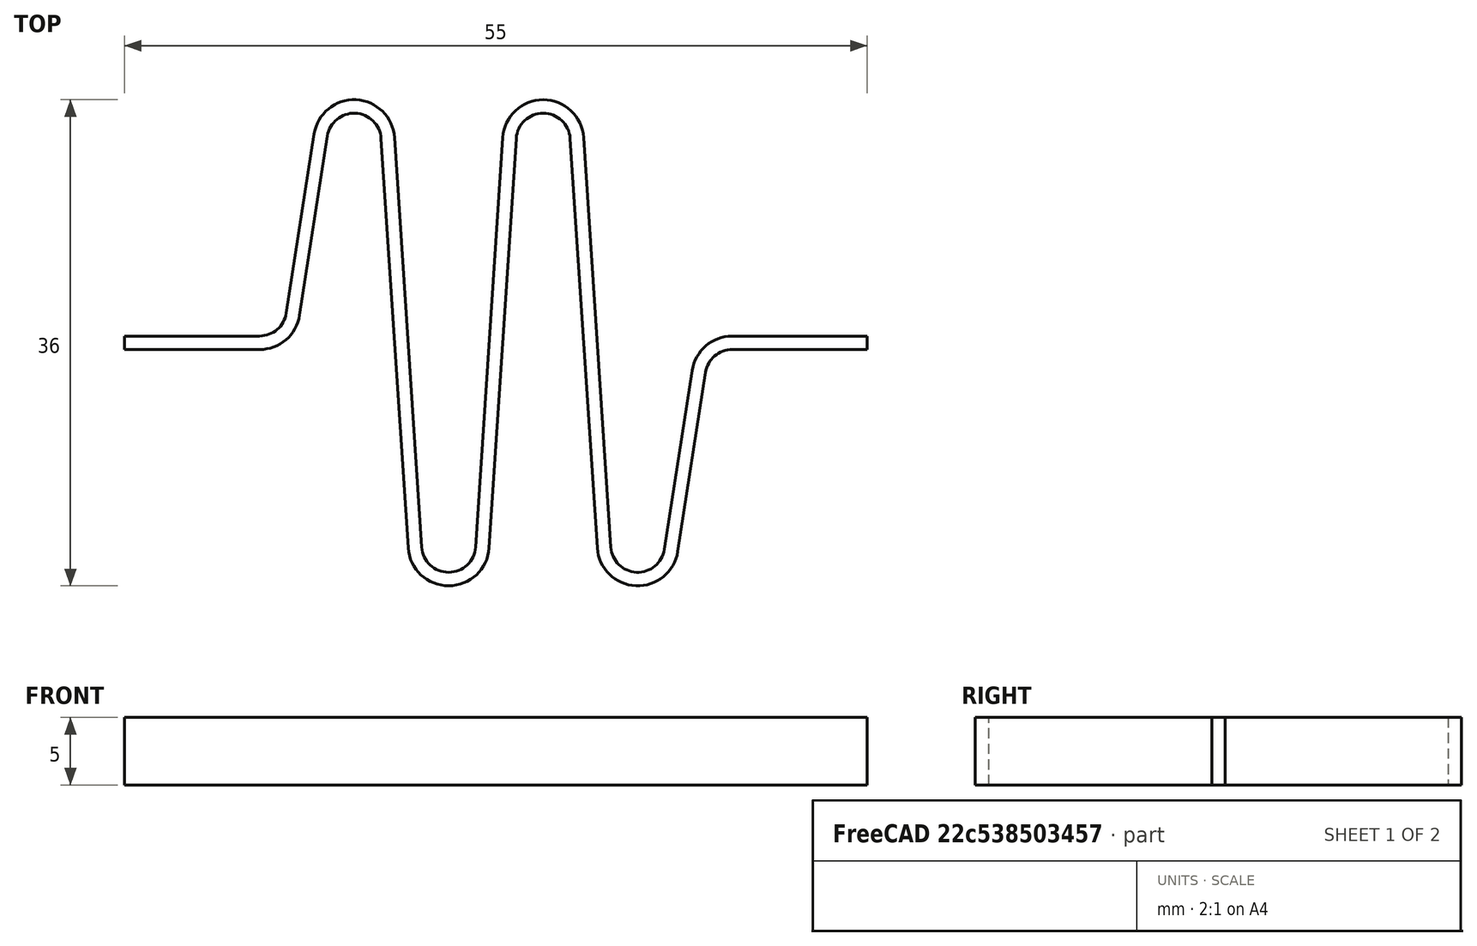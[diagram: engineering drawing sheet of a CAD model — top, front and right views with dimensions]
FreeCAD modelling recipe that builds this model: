
FCSTD DOCUMENT  (FreeCAD 2021.1015R24301 +3962 (Git))
Label: plastic_spring_1
License: All rights reserved
objects: Sketcher::SketchObject×2, Spreadsheet::Sheet×1, PartDesign::AdditivePipe×1, PartDesign::Body×1
note: 6 computed .brp shape members not serialized (recipe doc carries the construction recipe); baked Part::Feature solids carry a one-line shape summary decoded from their .brp

FEATURE [Spreadsheet::Sheet] Spreadsheet
  PythonMode = false
  cells = A1='height; B1(h)=5; A2='thickness; B2(thk)=1; A3='dia; B3(dia)=5; A4=center length; B4(l_center)=30; A5=center spacing; B5(cs)=7; C5=should be dia/2 really; A6=end length; B6(l_end)=10
FEATURE [Sketcher::SketchObject] Sketch  label="profile"
  FullyConstrained = true
  MapMode = 5
  Placement = pos=(0,0,0) rot=(0.57735,0.57735,0.57735;2.0944rad)
  Support = -> [YZ_Plane]
  expr: Constraints[10] = Spreadsheet.thk / 2
  expr: Constraints[11] = Spreadsheet.thk
  expr: Constraints[9] = Spreadsheet.h
  sketch-geometry (4):
    g0: LineSegment StartX=-0.5 StartY=0 StartZ=0 EndX=0.5 EndY=0 EndZ=0
    g1: LineSegment StartX=0.5 StartY=0 StartZ=0 EndX=0.5 EndY=5 EndZ=0
    g2: LineSegment StartX=0.5 StartY=5 StartZ=0 EndX=-0.5 EndY=5 EndZ=0
    g3: LineSegment StartX=-0.5 StartY=5 StartZ=0 EndX=-0.5 EndY=0 EndZ=0
  constraints (12):
    c: Coincident(g0,g1)
    c: Coincident(g1,g2)
    c: Coincident(g2,g3)
    c: Coincident(g3,g0)
    c: Horizontal(g0)
    c: Horizontal(g2)
    c: Vertical(g1)
    c: Vertical(g3)
    c: PointOnObject(g0,g-1)
    c: DistanceY(g3,g3) = 5
    c: DistanceX(g0,g-1) = 0.5
    c: DistanceX(g0,g0) = 1
FEATURE [Sketcher::SketchObject] Sketch001  label="path"
  FullyConstrained = false
  MapMode = 5
  Support = -> [XY_Plane]
  expr: Constraints[28] = Spreadsheet.l_end
  expr: Constraints[33] = Spreadsheet.l_center / 2
  expr: Constraints[34] = Spreadsheet.l_center
  expr: Constraints[39] = Spreadsheet.dia
  expr: Constraints[40] = Spreadsheet.dia
  expr: Constraints[41] = Spreadsheet.dia
  expr: Constraints[42] = Spreadsheet.dia
  expr: Constraints[43] = Spreadsheet.dia
  expr: Constraints[44] = Spreadsheet.dia
  expr: Constraints[45] = Spreadsheet.l_end
  expr: Constraints[46] = Spreadsheet.cs
  expr: Constraints[47] = Spreadsheet.cs
  expr: Constraints[48] = Spreadsheet.cs
  expr: Constraints[49] = Spreadsheet.cs
  expr: Constraints[50] = Spreadsheet.cs
  sketch-geometry (15):
    g0: LineSegment StartX=0 StartY=0 StartZ=0 EndX=10 EndY=0 EndZ=0
    g1: LineSegment StartX=12.4704 StartY=2.11657 StartZ=0 EndX=14.5296 EndY=15.3834 EndZ=0
    g2: ArcOfCircle CenterX=9.99998 CenterY=2.5 CenterZ=0 NormalX=0 NormalY=0 NormalZ=1 AngleXU=0 Radius=2.5 StartAngle=4.7124 EndAngle=6.1292
    g3: ArcOfCircle CenterX=17 CenterY=15 CenterZ=0 NormalX=0 NormalY=0 NormalZ=1 AngleXU=0 Radius=2.5 StartAngle=0.0662045 EndAngle=2.98761
    g4: LineSegment StartX=19.4945 StartY=15.1654 StartZ=0 EndX=21.5055 EndY=-15.1654 EndZ=0
    g5: ArcOfCircle CenterX=24 CenterY=-15 CenterZ=0 NormalX=0 NormalY=0 NormalZ=1 AngleXU=0 Radius=2.5 StartAngle=3.2078 EndAngle=6.21698
    g6: LineSegment StartX=26.4945 StartY=-15.1654 StartZ=0 EndX=28.5055 EndY=15.1654 EndZ=0
    g7: ArcOfCircle CenterX=31 CenterY=15 CenterZ=0 NormalX=0 NormalY=0 NormalZ=1 AngleXU=0 Radius=2.5 StartAngle=0.0662037 EndAngle=3.07539
    g8: LineSegment StartX=33.4945 StartY=15.1654 StartZ=0 EndX=35.5055 EndY=-15.1654 EndZ=0
    g9: ArcOfCircle CenterX=38 CenterY=-15 CenterZ=0 NormalX=0 NormalY=0 NormalZ=1 AngleXU=0 Radius=2.5 StartAngle=3.2078 EndAngle=6.1292
    g10: LineSegment StartX=40.4704 StartY=-15.3834 StartZ=0 EndX=42.5296 EndY=-2.11657 EndZ=0
    g11: LineSegment StartX=45 StartY=-9.89027e-11 StartZ=0 EndX=55 EndY=0 EndZ=0
    g12: ArcOfCircle CenterX=45 CenterY=-2.5 CenterZ=0 NormalX=0 NormalY=0 NormalZ=1 AngleXU=0 Radius=2.5 StartAngle=1.57081 EndAngle=2.98761
    g13: LineSegment [constr] StartX=0 StartY=15 StartZ=0 EndX=15.5655 EndY=15 EndZ=0
    g14: LineSegment [constr] StartX=0 StartY=-15 StartZ=0 EndX=16.0762 EndY=-15 EndZ=0
  constraints (51):
    c: Coincident(g0,g-1)
    c: PointOnObject(g0,g-1)
    c: Coincident(g2,g0)
    c: Coincident(g2,g1)
    c: Coincident(g3,g1)
    c: Coincident(g4,g3)
    c: Coincident(g5,g4)
    c: Coincident(g6,g5)
    c: Coincident(g7,g6)
    c: Coincident(g8,g7)
    c: Coincident(g9,g8)
    c: Coincident(g10,g9)
    c: PointOnObject(g11,g-1)
    c: PointOnObject(g11,g-1)
    c: Coincident(g12,g10)
    c: Coincident(g12,g11)
    c: Tangent(g0,g2)
    c: Tangent(g2,g1)
    c: Tangent(g1,g3)
    c: Tangent(g3,g4)
    c: Tangent(g4,g5)
    c: Tangent(g5,g6)
    c: Tangent(g6,g7)
    c: Tangent(g7,g8)
    c: Tangent(g9,g8)
    c: Tangent(g9,g10)
    c: Tangent(g10,g12)
    c: Tangent(g12,g11)
    c: DistanceX(g11,g11) = 10
    c: PointOnObject(g13,g-2)
    c: Horizontal(g13)
    c: PointOnObject(g14,g-2)
    c: Horizontal(g14)
    c: DistanceY(g0,g13) = 15
    c: DistanceY(g14,g13) = 30
    c: PointOnObject(g3,g13)
    c: PointOnObject(g5,g14)
    c: PointOnObject(g7,g13)
    c: PointOnObject(g9,g14)
    c: Diameter(g9) = 5
    c: Diameter(g7) = 5
    c: Diameter(g5) = 5
    c: Diameter(g12) = 5
    c: Diameter(g3) = 5
    c: Diameter(g2) = 5
    c: DistanceX(g0,g0) = 10
    c: DistanceX(g2,g3) = 7
    c: DistanceX(g3,g5) = 7
    c: DistanceX(g5,g7) = 7
    c: DistanceX(g7,g9) = 7
    c: DistanceX(g9,g12) = 7
FEATURE [PartDesign::AdditivePipe] AdditivePipe
  AuxilleryCurvelinear = true
  AuxillerySpineTangent = false
  Binormal = (0,0,0)
  ClaimChildren = false
  Fit = 0
  FitJoin = 0
  InnerFit = 0
  InnerFitJoin = 0
  Mode = 0
  NewSolid = false
  Placement = pos=(0,0,0) rot=(0.57735,0.57735,0.57735;2.0944rad)
  Profile = -> Sketch
  Spine = -> Sketch001
  SpineTangent = false
  Suppress = false
  Transformation = 0
  Transition = 1
  _ProfileBasedVersion = 1
FEATURE [PartDesign::Body] Body
  AutoGroupSolids = false
  ExportMode = 0
  Group = -> [Sketch,Sketch001,AdditivePipe]
  Origin = -> Origin
  Tip = -> AdditivePipe
  _ExportChildren = -> [AdditivePipe]
  _GroupVersion = 1
